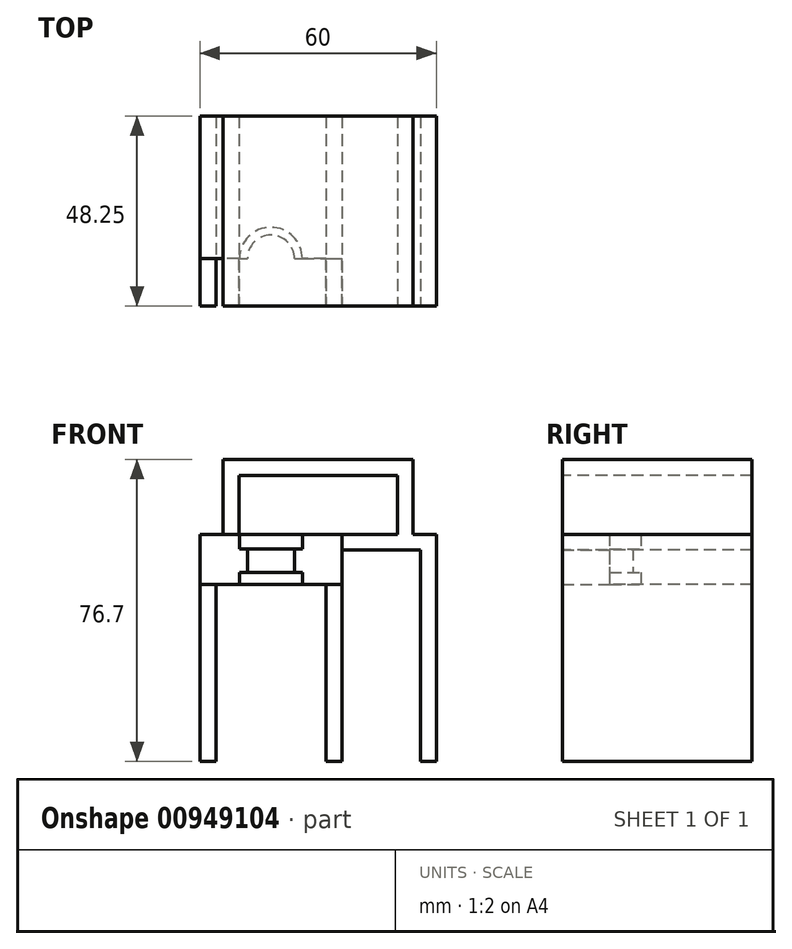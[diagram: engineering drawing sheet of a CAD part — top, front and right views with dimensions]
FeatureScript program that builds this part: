
annotation { "Feature Type Name" : "Feature", "Feature Type Description" : "" }
export const myFeature = defineFeature(function(context is Context, id is Id, definition is map)
    precondition{}
    {
        {
            assignVariable(context, id + "F0", {"name" : "tolerance_xy", "anyValue" : 0.25});
        }
        {
            var Q0;
            Q0=qCreatedBy(makeId("Front.planeOp"),FACE);
            var sketch = newSketch(context, id + "F1", { "sketchPlane" : qUnion([Q0])});
            skLineSegment(sketch, "E0.bottom", {"start": v(24.12, 2) * mm, "end": v(-24.12, 2) * mm});
            skLineSegment(sketch, "E0.top", {"start": v(24.12, -2) * mm, "end": v(-24.12, -2) * mm});
            skLineSegment(sketch, "E0.left", {"start": v(24.12, 2) * mm, "end": v(24.12, -2) * mm});
            skLineSegment(sketch, "E0.right", {"start": v(-24.12, 2) * mm, "end": v(-24.12, -2) * mm});
            skPoint(sketch, "E0.middle", {"position": v(0, 0) * mm});
            skLineSegment(sketch, "E1", {"start": v(0, 2) * mm, "end": v(0, -2) * mm, "construction": true});
            skLineSegment(sketch, "E2", {"start": v(-12, 2) * mm, "end": v(-12, -2) * mm, "construction": true});
            skLineSegment(sketch, "E3.bottom", {"start": v(-0.85, -29.7) * mm, "end": v(-23.15, -29.7) * mm});
            skLineSegment(sketch, "E3.top", {"start": v(-0.85, -59.7) * mm, "end": v(-23.15, -59.7) * mm});
            skLineSegment(sketch, "E3.left", {"start": v(-0.85, -29.7) * mm, "end": v(-0.85, -59.7) * mm});
            skLineSegment(sketch, "E3.right", {"start": v(-23.15, -29.7) * mm, "end": v(-23.15, -59.7) * mm});
            skPoint(sketch, "E3.middle", {"position": v(-12, -44.7) * mm});
            skLineSegment(sketch, "E4.bottom", {"start": v(-4, -29.7) * mm, "end": v(-20, -29.7) * mm});
            skLineSegment(sketch, "E4.top", {"start": v(-4, -26.7) * mm, "end": v(-20, -26.7) * mm});
            skLineSegment(sketch, "E4.left", {"start": v(-4, -29.7) * mm, "end": v(-4, -26.7) * mm});
            skLineSegment(sketch, "E4.right", {"start": v(-20, -29.7) * mm, "end": v(-20, -26.7) * mm});
            skPoint(sketch, "E4.middle", {"position": v(-12, -28.2) * mm});
            skLineSegment(sketch, "E5.bottom", {"start": v(-6, -26.7) * mm, "end": v(-18, -26.7) * mm});
            skLineSegment(sketch, "E5.top", {"start": v(-6, -20.7) * mm, "end": v(-18, -20.7) * mm});
            skLineSegment(sketch, "E5.left", {"start": v(-6, -26.7) * mm, "end": v(-6, -20.7) * mm});
            skLineSegment(sketch, "E5.right", {"start": v(-18, -26.7) * mm, "end": v(-18, -20.7) * mm});
            skPoint(sketch, "E5.middle", {"position": v(-12, -23.7) * mm});
            skLineSegment(sketch, "E6.bottom", {"start": v(-4, -20.7) * mm, "end": v(-20, -20.7) * mm});
            skLineSegment(sketch, "E6.top", {"start": v(-4, -17) * mm, "end": v(-20, -17) * mm});
            skLineSegment(sketch, "E6.left", {"start": v(-4, -20.7) * mm, "end": v(-4, -17) * mm});
            skLineSegment(sketch, "E6.right", {"start": v(-20, -20.7) * mm, "end": v(-20, -17) * mm});
            skPoint(sketch, "E6.middle", {"position": v(-12, -18.85) * mm});
            skLineSegment(sketch, "E7.bottom", {"start": v(-4, -59.7) * mm, "end": v(-20, -59.7) * mm});
            skLineSegment(sketch, "E7.top", {"start": v(-4, -79.3) * mm, "end": v(-20, -79.3) * mm});
            skLineSegment(sketch, "E7.left", {"start": v(-4, -59.7) * mm, "end": v(-4, -79.3) * mm});
            skLineSegment(sketch, "E7.right", {"start": v(-20, -59.7) * mm, "end": v(-20, -79.3) * mm});
            skPoint(sketch, "E7.middle", {"position": v(-12, -69.5) * mm});
            skPoint(sketch, "E7.middle.positionSnap0", {"position": v(-12, -59.7) * mm});
            skPoint(sketch, "E7.centerSnap0", {"position": v(-12, -59.7) * mm});
            skLineSegment(sketch, "E8", {"start": v(-4, -17) * mm, "end": v(24.13, -17) * mm});
            skLineSegment(sketch, "E9", {"start": v(-20, -17) * mm, "end": v(-24.12, -17) * mm});
            skLineSegment(sketch, "E10", {"start": v(20.13, -17) * mm, "end": v(20.13, -2) * mm});
            skLineSegment(sketch, "E11", {"start": v(-20.12, -2) * mm, "end": v(-20.12, -17) * mm});
            skLineSegment(sketch, "E12", {"start": v(-24.12, -17) * mm, "end": v(-24.12, -2) * mm});
            skLineSegment(sketch, "E13", {"start": v(24.13, -17) * mm, "end": v(24.12, -2) * mm});
            skLineSegment(sketch, "E14", {"start": v(-24.12, -17) * mm, "end": v(-30, -17) * mm});
            skLineSegment(sketch, "E15", {"start": v(-30, -17) * mm, "end": v(-30, -29.7) * mm});
            skLineSegment(sketch, "E16", {"start": v(6, -17) * mm, "end": v(6, -29.7) * mm});
            skLineSegment(sketch, "E17", {"start": v(-23.15, -29.7) * mm, "end": v(-30, -29.7) * mm});
            skLineSegment(sketch, "E18", {"start": v(-0.85, -29.7) * mm, "end": v(6, -29.7) * mm});
            skLineSegment(sketch, "E19", {"start": v(0, -2) * mm, "end": v(0, -17) * mm, "construction": true});
            skLineSegment(sketch, "E20", {"start": v(24.13, -17) * mm, "end": v(24.13, -21) * mm});
            skLineSegment(sketch, "E21", {"start": v(24.13, -21) * mm, "end": v(6, -21) * mm});
            skLineSegment(sketch, "E22", {"start": v(-12, -17) * mm, "end": v(-12, -79.3) * mm});
            skLineSegment(sketch, "E23", {"start": v(-30, -29.7) * mm, "end": v(-30, -74.7) * mm});
            skLineSegment(sketch, "E24", {"start": v(-30, -74.7) * mm, "end": v(-26, -74.7) * mm});
            skLineSegment(sketch, "E25", {"start": v(-26, -74.7) * mm, "end": v(-26, -29.7) * mm});
            skLineSegment(sketch, "E26", {"start": v(24.13, -17) * mm, "end": v(30, -17) * mm});
            skLineSegment(sketch, "E27", {"start": v(30, -17) * mm, "end": v(30, -74.7) * mm});
            skLineSegment(sketch, "E28", {"start": v(30, -74.7) * mm, "end": v(26, -74.7) * mm});
            skLineSegment(sketch, "E29", {"start": v(26, -74.7) * mm, "end": v(26, -21) * mm});
            skLineSegment(sketch, "E30", {"start": v(26, -21) * mm, "end": v(24.13, -21) * mm});
            skLineSegment(sketch, "E31", {"start": v(16, 2) * mm, "end": v(16, -2) * mm, "construction": true});
            skLineSegment(sketch, "E32", {"start": v(16, -2) * mm, "end": v(16, -17) * mm, "construction": true});
            skLineSegment(sketch, "E33", {"start": v(16, -17) * mm, "end": v(16, -21) * mm, "construction": true});
            skLineSegment(sketch, "E34", {"start": v(16, -21) * mm, "end": v(16, -79.3) * mm, "construction": true});
            skLineSegment(sketch, "E35.bottom", {"start": v(20, -78.3) * mm, "end": v(12, -78.3) * mm});
            skLineSegment(sketch, "E35.top", {"start": v(20, -28.3) * mm, "end": v(12, -28.3) * mm});
            skLineSegment(sketch, "E35.left", {"start": v(20, -78.3) * mm, "end": v(20, -28.3) * mm});
            skLineSegment(sketch, "E35.right", {"start": v(12, -78.3) * mm, "end": v(12, -28.3) * mm});
            skPoint(sketch, "E35.middle", {"position": v(16, -53.3) * mm});
            skLineSegment(sketch, "E36", {"start": v(6, -29.7) * mm, "end": v(6, -74.7) * mm});
            skLineSegment(sketch, "E37", {"start": v(6, -74.7) * mm, "end": v(2, -74.7) * mm});
            skLineSegment(sketch, "E38", {"start": v(2, -74.7) * mm, "end": v(2, -29.7) * mm});
            skLineSegment(sketch, "E39", {"start": v(-12, -2) * mm, "end": v(-12, -17) * mm, "construction": true});
            skSolve(sketch);
        }
        {
            var Q0;
            Q0=makeQuery(id+"F1.imprint","IMPRINT",FACE,{"disambiguationData":[TD([[makeQuery(id+"F1.imprint","IMPRINT",EDGE,{"derivedFrom":sQuery(id+"F1.wireOp",EDGE,"EVi3CAAb-2JPS-dWWF-iVDz-TEHDUSdwfeNA")}),-1.0]])]});
            var Q1;
            Q1=makeQuery(id+"F1.imprint","IMPRINT",FACE,{"disambiguationData":[TD([[makeQuery(id+"F1.imprint","IMPRINT",EDGE,{"derivedFrom":sQuery(id+"F1.wireOp",EDGE,"li1ah5QJ-acof-ilof-ebTE-JALTnLC66vGA")}),1.0]])]});
            var Q2;
            {var subQ6=sQuery(id+"F1.wireOp",EDGE,"z5uiTYtQ-MssI-6U3G-QtEK-OVCcDuCMIT78");Q2=makeQuery(id+"F1.imprint","IMPRINT",FACE,{"disambiguationData":[TD([[makeQuery(id+"F1.imprint","IMPRINT",EDGE,{"derivedFrom":subQ6}),-1.0]])]});}
            var Q3;
            Q3=makeQuery(id+"F1.imprint","IMPRINT",FACE,{"disambiguationData":[TD([[makeQuery(id+"F1.imprint","IMPRINT",EDGE,{"derivedFrom":sQuery(id+"F1.wireOp",EDGE,"E0.bottom")}),1.0]])]});
            var Q4;
            {var subQ4=sQuery(id+"F1.wireOp",EDGE,"z5uiTYtQ-MssI-6U3G-QtEK-OVCcDuCMIT78");Q4=makeQuery(id+"F1.imprint","IMPRINT",FACE,{"disambiguationData":[TD([[makeQuery(id+"F1.imprint","IMPRINT",EDGE,{"derivedFrom":subQ4}),1.0]])]});}
            var Q5;
            {var subQ0=sQuery(id+"F1.wireOp",EDGE,"mifTbPQZ-43xI-ZBlQ-VLPK-ncA9iN9dikbS");Q5=makeQuery(id+"F1.imprint","IMPRINT",FACE,{"disambiguationData":[TD([[makeQuery(id+"F1.imprint","IMPRINT",EDGE,{"derivedFrom":subQ0}),1.0]])]});}
            var Q6;
            {var subQ0=sQuery(id+"F1.wireOp",EDGE,"wzDDLQLR-NU49-GX1u-ui8f-UiJYlwX41QNS");Q6=makeQuery(id+"F1.imprint","IMPRINT",FACE,{"disambiguationData":[TD([[makeQuery(id+"F1.imprint","IMPRINT",EDGE,{"derivedFrom":subQ0}),-1.0]])]});}
            var Q7;
            {var subQ2=sQuery(id+"F1.wireOp",EDGE,"E11");Q7=makeQuery(id+"F1.imprint","IMPRINT",FACE,{"disambiguationData":[TD([[makeQuery(id+"F1.imprint","IMPRINT",EDGE,{"derivedFrom":subQ2}),-1.0]])]});}
            var Q8;
            {var subQ0=sQuery(id+"F1.wireOp",EDGE,"E10");Q8=makeQuery(id+"F1.imprint","IMPRINT",FACE,{"disambiguationData":[TD([[makeQuery(id+"F1.imprint","IMPRINT",EDGE,{"derivedFrom":subQ0}),-1.0]])]});}
            var Q9;
            {var subQ0=sQuery(id+"F1.wireOp",EDGE,"E20");Q9=makeQuery(id+"F1.imprint","IMPRINT",FACE,{"disambiguationData":[TD([[makeQuery(id+"F1.imprint","IMPRINT",EDGE,{"derivedFrom":subQ0}),-1.0]])]});}
            var Q10;
            {var subQ11=sQuery(id+"F1.wireOp",EDGE,"E4.left");Q10=makeQuery(id+"F1.imprint","IMPRINT",FACE,{"disambiguationData":[TD([[makeQuery(id+"F1.imprint","IMPRINT",EDGE,{"derivedFrom":subQ11}),-1.0]])]});}
            var Q11;
            {var subQ11=sQuery(id+"F1.wireOp",EDGE,"E4.right");Q11=makeQuery(id+"F1.imprint","IMPRINT",FACE,{"disambiguationData":[TD([[makeQuery(id+"F1.imprint","IMPRINT",EDGE,{"derivedFrom":subQ11}),1.0]])]});}
            var Q12;
            {var subQ0=sQuery(id+"F1.wireOp",EDGE,"E6.right");var subQ9=sQuery(id+"F1.wireOp",EDGE,"E6.left");Q12=qUnion([makeQuery(id+"F1.imprint","IMPRINT",FACE,{"disambiguationData":[TD([[makeQuery(id+"F1.imprint","IMPRINT",EDGE,{"derivedFrom":subQ9}),1.0]])]}),makeQuery(id+"F1.imprint","IMPRINT",FACE,{"disambiguationData":[TD([[makeQuery(id+"F1.imprint","IMPRINT",EDGE,{"derivedFrom":subQ0}),-1.0]])]})]);}
            var Q13;
            {var subQ3=sQuery(id+"F1.wireOp",EDGE,"E5.left");var subQ8=sQuery(id+"F1.wireOp",EDGE,"E5.right");Q13=qUnion([makeQuery(id+"F1.imprint","IMPRINT",FACE,{"disambiguationData":[TD([[makeQuery(id+"F1.imprint","IMPRINT",EDGE,{"derivedFrom":subQ8}),-1.0]])]}),makeQuery(id+"F1.imprint","IMPRINT",FACE,{"disambiguationData":[TD([[makeQuery(id+"F1.imprint","IMPRINT",EDGE,{"derivedFrom":subQ3}),1.0]])]})]);}
            var Q14;
            {var subQ0=sQuery(id+"F1.wireOp",EDGE,"E4.left");var subQ8=sQuery(id+"F1.wireOp",EDGE,"E4.right");Q14=qUnion([makeQuery(id+"F1.imprint","IMPRINT",FACE,{"disambiguationData":[TD([[makeQuery(id+"F1.imprint","IMPRINT",EDGE,{"derivedFrom":subQ8}),-1.0]])]}),makeQuery(id+"F1.imprint","IMPRINT",FACE,{"disambiguationData":[TD([[makeQuery(id+"F1.imprint","IMPRINT",EDGE,{"derivedFrom":subQ0}),1.0]])]})]);}
            var Q15;
            Q15=makeQuery(id+"F1.imprint","IMPRINT",FACE,{"disambiguationData":[TD([[makeQuery(id+"F1.imprint","IMPRINT",EDGE,{"derivedFrom":sQuery(id+"F1.wireOp",EDGE,"E15")}),-1.0]])]});
            var Q16;
            Q16=makeQuery(id+"F1.imprint","IMPRINT",FACE,{"disambiguationData":[TD([[makeQuery(id+"F1.imprint","IMPRINT",EDGE,{"derivedFrom":sQuery(id+"F1.wireOp",EDGE,"dNWT3YAO-GiWa-Cg9N-cAbu-C3DIynb8dIXF")}),1.0]])]});
            var Q17;
            Q17=makeQuery(id+"F1.imprint","IMPRINT",FACE,{"disambiguationData":[TD([[makeQuery(id+"F1.imprint","IMPRINT",EDGE,{"derivedFrom":sQuery(id+"F1.wireOp",EDGE,"E20")}),1.0]])]});
            var Q18;
            {var subQ0=sQuery(id+"F1.wireOp",EDGE,"cKC2Mqy2-LGOq-yzxD-5E3b-RmwVXZnaAdVm");Q18=makeQuery(id+"F1.imprint","IMPRINT",FACE,{"disambiguationData":[TD([[makeQuery(id+"F1.imprint","IMPRINT",EDGE,{"derivedFrom":subQ0}),-1.0]])]});}
            var Q19;
            {var subQ0=sQuery(id+"F1.wireOp",EDGE,"gX3H04Mc-1Ecm-lcYE-YZgx-7ilmu9O8GNxG");Q19=makeQuery(id+"F1.imprint","IMPRINT",FACE,{"disambiguationData":[TD([[makeQuery(id+"F1.imprint","IMPRINT",EDGE,{"derivedFrom":subQ0}),1.0]])]});}
            var Q20;
            Q20=makeQuery(id+"F1.imprint","IMPRINT",FACE,{"disambiguationData":[TD([[makeQuery(id+"F1.imprint","IMPRINT",EDGE,{"derivedFrom":sQuery(id+"F1.wireOp",EDGE,"9OMSy0bi-BGxA-zATD-53jt-BObqU4ymDjqa")}),1.0]])]});
            var Q21;
            Q21=makeQuery(id+"F1.imprint","IMPRINT",FACE,{"disambiguationData":[TD([[makeQuery(id+"F1.imprint","IMPRINT",EDGE,{"derivedFrom":sQuery(id+"F1.wireOp",EDGE,"IGTo2MxJ-7poq-D3uY-cPep-3G9ocuP2SsBW")}),1.0]])]});
            var Q22;
            Q22=makeQuery(id+"F1.imprint","IMPRINT",FACE,{"disambiguationData":[TD([[makeQuery(id+"F1.imprint","IMPRINT",EDGE,{"derivedFrom":sQuery(id+"F1.wireOp",EDGE,"Q3cqwPKf-kPYn-MF6c-oUdf-HiEDPvpDas5v")}),-1.0]])]});
            var Q23;
            Q23=makeQuery(id+"F1.imprint","IMPRINT",FACE,{"disambiguationData":[TD([[makeQuery(id+"F1.imprint","IMPRINT",EDGE,{"derivedFrom":sQuery(id+"F1.wireOp",EDGE,"fqccvdEp-aMlx-VEsP-pl86-uqnwdZdXVRP9")}),-1.0]])]});
            var Q24;
            {var subQ0=sQuery(id+"F1.wireOp",EDGE,"fzIKRdge-Mkhf-AST9-Wr0f-vCw1WpWpjTyl");Q24=makeQuery(id+"F1.imprint","IMPRINT",FACE,{"disambiguationData":[TD([[makeQuery(id+"F1.imprint","IMPRINT",EDGE,{"derivedFrom":subQ0}),-1.0]])]});}
            var Q25;
            {var subQ0=sQuery(id+"F1.wireOp",EDGE,"E23");Q25=makeQuery(id+"F1.imprint","IMPRINT",FACE,{"disambiguationData":[TD([[makeQuery(id+"F1.imprint","IMPRINT",EDGE,{"derivedFrom":subQ0}),1.0]])]});}
            var Q26;
            {var subQ2=sQuery(id+"F1.wireOp",EDGE,"E36");Q26=makeQuery(id+"F1.imprint","IMPRINT",FACE,{"disambiguationData":[TD([[makeQuery(id+"F1.imprint","IMPRINT",EDGE,{"derivedFrom":subQ2}),-1.0]])]});}
            extrude(context, id + "F2", {"entities" : qUnion([Q0, Q1, Q2, Q3, Q4, Q5, Q6, Q7, Q8, Q9, Q10, Q11, Q12, Q13, Q14, Q15, Q16, Q17, Q18, Q19, Q20, Q21, Q22, Q23, Q24, Q25, Q26]), "oppositeDirection" : true, "depth" : (48 - 12 + getVariable(context, 'tolerance_xy')) * mm, "offsetDistance" : 25 * mm, "hasSecondDirection" : true, "secondDirectionOppositeDirection" : true, "secondDirectionDepth" : 0 * mm});
        }
        {
            var Q0;
            {var subQ0=sQuery(id+"F1.wireOp",EDGE,"E6.right");Q0=makeQuery(id+"F1.imprint","IMPRINT",FACE,{"disambiguationData":[TD([[makeQuery(id+"F1.imprint","IMPRINT",EDGE,{"derivedFrom":subQ0}),-1.0]])]});}
            var Q1;
            {var subQ3=sQuery(id+"F1.wireOp",EDGE,"E5.right");Q1=makeQuery(id+"F1.imprint","IMPRINT",FACE,{"disambiguationData":[TD([[makeQuery(id+"F1.imprint","IMPRINT",EDGE,{"derivedFrom":subQ3}),-1.0]])]});}
            var Q2;
            {var subQ0=sQuery(id+"F1.wireOp",EDGE,"E4.right");Q2=makeQuery(id+"F1.imprint","IMPRINT",FACE,{"disambiguationData":[TD([[makeQuery(id+"F1.imprint","IMPRINT",EDGE,{"derivedFrom":subQ0}),-1.0]])]});}
            var Q3;
            Q3=sQuery(id+"F1.wireOp",EDGE,"E22");
            revolve(context, id + "F3", {"operationType" : NewBodyOperationType.REMOVE, "surfaceOperationType" : NewSurfaceOperationType.NEW, "entities" : qUnion([Q0, Q1, Q2]), "axis" : qUnion([Q3]), "revolveType" : RevolveType.FULL, "oppositeDirection" : true});
        }
        {
            var Q0;
            Q0=makeQuery(id+"F1.imprint","IMPRINT",FACE,{"disambiguationData":[TD([[makeQuery(id+"F1.imprint","IMPRINT",EDGE,{"derivedFrom":sQuery(id+"F1.wireOp",EDGE,"E15")}),-1.0]])]});
            var Q1;
            {var subQ0=sQuery(id+"F1.wireOp",EDGE,"gX3H04Mc-1Ecm-lcYE-YZgx-7ilmu9O8GNxG");Q1=makeQuery(id+"F1.imprint","IMPRINT",FACE,{"disambiguationData":[TD([[makeQuery(id+"F1.imprint","IMPRINT",EDGE,{"derivedFrom":subQ0}),1.0]])]});}
            var Q2;
            Q2=makeQuery(id+"F1.imprint","IMPRINT",FACE,{"disambiguationData":[TD([[makeQuery(id+"F1.imprint","IMPRINT",EDGE,{"derivedFrom":sQuery(id+"F1.wireOp",EDGE,"IGTo2MxJ-7poq-D3uY-cPep-3G9ocuP2SsBW")}),1.0]])]});
            var Q3;
            Q3=makeQuery(id+"F1.imprint","IMPRINT",FACE,{"disambiguationData":[TD([[makeQuery(id+"F1.imprint","IMPRINT",EDGE,{"derivedFrom":sQuery(id+"F1.wireOp",EDGE,"9OMSy0bi-BGxA-zATD-53jt-BObqU4ymDjqa")}),1.0]])]});
            var Q4;
            {var subQ2=sQuery(id+"F1.wireOp",EDGE,"E11");Q4=makeQuery(id+"F1.imprint","IMPRINT",FACE,{"disambiguationData":[TD([[makeQuery(id+"F1.imprint","IMPRINT",EDGE,{"derivedFrom":subQ2}),-1.0]])]});}
            var Q5;
            Q5=makeQuery(id+"F1.imprint","IMPRINT",FACE,{"disambiguationData":[TD([[makeQuery(id+"F1.imprint","IMPRINT",EDGE,{"derivedFrom":sQuery(id+"F1.wireOp",EDGE,"E0.bottom")}),1.0]])]});
            var Q6;
            {var subQ0=sQuery(id+"F1.wireOp",EDGE,"E10");Q6=makeQuery(id+"F1.imprint","IMPRINT",FACE,{"disambiguationData":[TD([[makeQuery(id+"F1.imprint","IMPRINT",EDGE,{"derivedFrom":subQ0}),-1.0]])]});}
            var Q7;
            {var subQ0=sQuery(id+"F1.wireOp",EDGE,"E20");Q7=makeQuery(id+"F1.imprint","IMPRINT",FACE,{"disambiguationData":[TD([[makeQuery(id+"F1.imprint","IMPRINT",EDGE,{"derivedFrom":subQ0}),-1.0]])]});}
            var Q8;
            Q8=makeQuery(id+"F1.imprint","IMPRINT",FACE,{"disambiguationData":[TD([[makeQuery(id+"F1.imprint","IMPRINT",EDGE,{"derivedFrom":sQuery(id+"F1.wireOp",EDGE,"E20")}),1.0]])]});
            var Q9;
            Q9=makeQuery(id+"F1.imprint","IMPRINT",FACE,{"disambiguationData":[TD([[makeQuery(id+"F1.imprint","IMPRINT",EDGE,{"derivedFrom":sQuery(id+"F1.wireOp",EDGE,"Q3cqwPKf-kPYn-MF6c-oUdf-HiEDPvpDas5v")}),-1.0]])]});
            var Q10;
            {var subQ0=sQuery(id+"F1.wireOp",EDGE,"cKC2Mqy2-LGOq-yzxD-5E3b-RmwVXZnaAdVm");Q10=makeQuery(id+"F1.imprint","IMPRINT",FACE,{"disambiguationData":[TD([[makeQuery(id+"F1.imprint","IMPRINT",EDGE,{"derivedFrom":subQ0}),-1.0]])]});}
            var Q11;
            Q11=makeQuery(id+"F1.imprint","IMPRINT",FACE,{"disambiguationData":[TD([[makeQuery(id+"F1.imprint","IMPRINT",EDGE,{"derivedFrom":sQuery(id+"F1.wireOp",EDGE,"dNWT3YAO-GiWa-Cg9N-cAbu-C3DIynb8dIXF")}),1.0]])]});
            var Q12;
            Q12=makeQuery(id+"F1.imprint","IMPRINT",FACE,{"disambiguationData":[TD([[makeQuery(id+"F1.imprint","IMPRINT",EDGE,{"derivedFrom":sQuery(id+"F1.wireOp",EDGE,"fqccvdEp-aMlx-VEsP-pl86-uqnwdZdXVRP9")}),-1.0]])]});
            var Q13;
            {var subQ0=sQuery(id+"F1.wireOp",EDGE,"fzIKRdge-Mkhf-AST9-Wr0f-vCw1WpWpjTyl");Q13=makeQuery(id+"F1.imprint","IMPRINT",FACE,{"disambiguationData":[TD([[makeQuery(id+"F1.imprint","IMPRINT",EDGE,{"derivedFrom":subQ0}),-1.0]])]});}
            var Q14;
            {var subQ0=sQuery(id+"F1.wireOp",EDGE,"E23");Q14=makeQuery(id+"F1.imprint","IMPRINT",FACE,{"disambiguationData":[TD([[makeQuery(id+"F1.imprint","IMPRINT",EDGE,{"derivedFrom":subQ0}),1.0]])]});}
            var Q15;
            {var subQ2=sQuery(id+"F1.wireOp",EDGE,"E36");Q15=makeQuery(id+"F1.imprint","IMPRINT",FACE,{"disambiguationData":[TD([[makeQuery(id+"F1.imprint","IMPRINT",EDGE,{"derivedFrom":subQ2}),-1.0]])]});}
            extrude(context, id + "F4", {"entities" : qUnion([Q0, Q1, Q2, Q3, Q4, Q5, Q6, Q7, Q8, Q9, Q10, Q11, Q12, Q13, Q14, Q15]), "operationType" : NewBodyOperationType.ADD, "depth" : 12 * mm, "offsetDistance" : 25 * mm});
        }
    });
